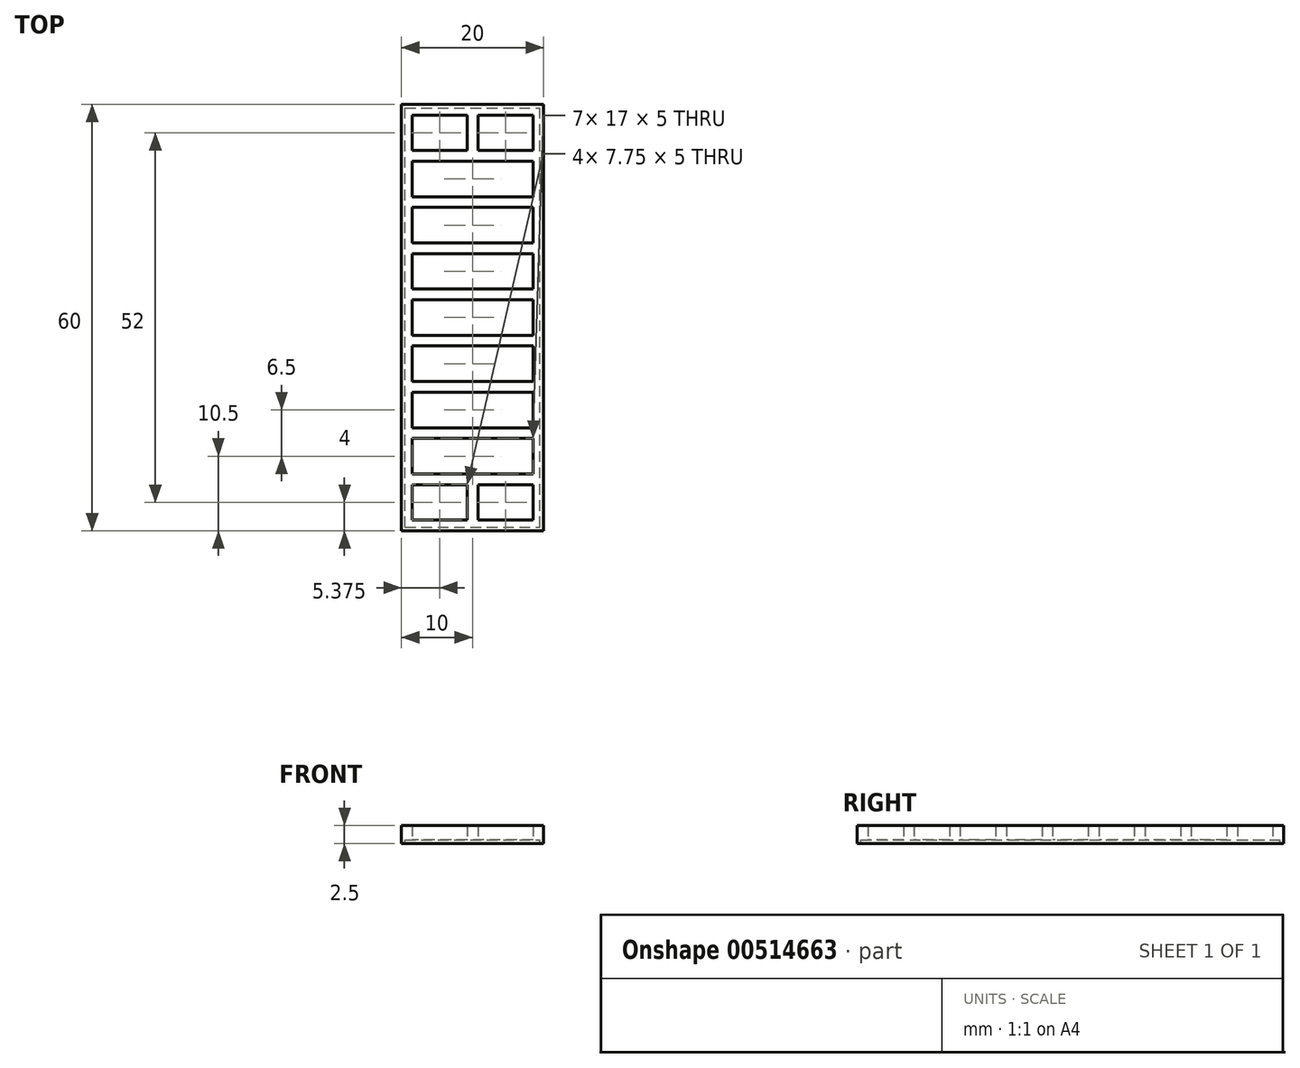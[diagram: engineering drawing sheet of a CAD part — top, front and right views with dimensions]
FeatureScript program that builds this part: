
annotation { "Feature Type Name" : "Feature", "Feature Type Description" : "" }
export const myFeature = defineFeature(function(context is Context, id is Id, definition is map)
    precondition{}
    {
        {
            var Q0;
            Q0=qCreatedBy(makeId("Top.planeOp"),FACE);
            var sketch = newSketch(context, id + "F0", { "sketchPlane" : qUnion([Q0])});
            skLineSegment(sketch, "E0.bottom", {"start": v(0, 0) * mm, "end": v(20, 0) * mm});
            skLineSegment(sketch, "E0.top", {"start": v(0, 60) * mm, "end": v(20, 60) * mm});
            skLineSegment(sketch, "E0.left", {"start": v(0, 0) * mm, "end": v(0, 60) * mm});
            skLineSegment(sketch, "E0.right", {"start": v(20, 0) * mm, "end": v(20, 60) * mm});
            skLineSegment(sketch, "E1.0", {"start": v(1.5, 1.5) * mm, "end": v(1.5, 6.5) * mm});
            skLineSegment(sketch, "E1.1", {"start": v(1.5, 1.5) * mm, "end": v(9.25, 1.5) * mm});
            skLineSegment(sketch, "E1.2", {"start": v(18.5, 1.5) * mm, "end": v(18.5, 6.5) * mm});
            skLineSegment(sketch, "E1.3", {"start": v(1.5, 58.5) * mm, "end": v(9.25, 58.5) * mm});
            skLineSegment(sketch, "E2", {"start": v(1.5, 53.5) * mm, "end": v(9.25, 53.5) * mm});
            skLineSegment(sketch, "E3", {"start": v(1.5, 52) * mm, "end": v(18.5, 52) * mm});
            skLineSegment(sketch, "E4.1.0.0", {"start": v(1.5, 47) * mm, "end": v(18.5, 47) * mm});
            skLineSegment(sketch, "E4.1.0.1", {"start": v(1.5, 45.5) * mm, "end": v(18.5, 45.5) * mm});
            skLineSegment(sketch, "E4.2.0.0", {"start": v(1.5, 40.5) * mm, "end": v(18.5, 40.5) * mm});
            skLineSegment(sketch, "E4.2.0.1", {"start": v(1.5, 39) * mm, "end": v(18.5, 39) * mm});
            skLineSegment(sketch, "E4.3.0.0", {"start": v(1.5, 34) * mm, "end": v(18.5, 34) * mm});
            skLineSegment(sketch, "E4.3.0.1", {"start": v(1.5, 32.5) * mm, "end": v(18.5, 32.5) * mm});
            skLineSegment(sketch, "E4.4.0.0", {"start": v(1.5, 27.5) * mm, "end": v(18.5, 27.5) * mm});
            skLineSegment(sketch, "E4.4.0.1", {"start": v(1.5, 26) * mm, "end": v(18.5, 26) * mm});
            skLineSegment(sketch, "E4.5.0.0", {"start": v(1.5, 21) * mm, "end": v(18.5, 21) * mm});
            skLineSegment(sketch, "E4.5.0.1", {"start": v(1.5, 19.5) * mm, "end": v(18.5, 19.5) * mm});
            skLineSegment(sketch, "E4.6.0.0", {"start": v(1.5, 14.5) * mm, "end": v(18.5, 14.5) * mm});
            skLineSegment(sketch, "E4.6.0.1", {"start": v(1.5, 13) * mm, "end": v(18.5, 13) * mm});
            skLineSegment(sketch, "E4.7.0.0", {"start": v(1.5, 8) * mm, "end": v(18.5, 8) * mm});
            skLineSegment(sketch, "E4.7.0.1", {"start": v(1.5, 6.5) * mm, "end": v(9.25, 6.5) * mm});
            skLineSegment(sketch, "E4.direction1", {"start": v(1.5, 52) * mm, "end": v(1.5, 47) * mm, "construction": true});
            skLineSegment(sketch, "E5", {"start": v(10.75, 58.5) * mm, "end": v(10.75, 53.5) * mm});
            skLineSegment(sketch, "E6", {"start": v(9.25, 58.5) * mm, "end": v(9.25, 53.5) * mm});
            skLineSegment(sketch, "E7", {"start": v(20, 30) * mm, "end": v(23.16, 30) * mm, "construction": true});
            skPoint(sketch, "E7.endSnap0", {"position": v(20, 30) * mm});
            skLineSegment(sketch, "E8.MirrorCS", {"start": v(10.75, 1.5) * mm, "end": v(10.75, 6.5) * mm});
            skLineSegment(sketch, "E9.MirrorCS", {"start": v(9.25, 1.5) * mm, "end": v(9.25, 6.5) * mm});
            skLineSegment(sketch, "E10.trimOffspring", {"start": v(10.75, 1.5) * mm, "end": v(18.5, 1.5) * mm});
            skLineSegment(sketch, "E11.trimOffspring", {"start": v(10.75, 6.5) * mm, "end": v(18.5, 6.5) * mm});
            skLineSegment(sketch, "E12.trimOffspring", {"start": v(18.5, 8) * mm, "end": v(18.5, 13) * mm});
            skLineSegment(sketch, "E13.trimOffspring", {"start": v(18.5, 14.5) * mm, "end": v(18.5, 19.5) * mm});
            skLineSegment(sketch, "E14.trimOffspring", {"start": v(1.5, 14.5) * mm, "end": v(1.5, 19.5) * mm});
            skLineSegment(sketch, "E15.trimOffspring", {"start": v(1.5, 8) * mm, "end": v(1.5, 13) * mm});
            skLineSegment(sketch, "E16.trimOffspring", {"start": v(18.5, 21) * mm, "end": v(18.5, 26) * mm});
            skLineSegment(sketch, "E17.trimOffspring", {"start": v(1.5, 21) * mm, "end": v(1.5, 26) * mm});
            skLineSegment(sketch, "E18.trimOffspring", {"start": v(1.5, 27.5) * mm, "end": v(1.5, 32.5) * mm});
            skLineSegment(sketch, "E19.trimOffspring", {"start": v(18.5, 27.5) * mm, "end": v(18.5, 32.5) * mm});
            skLineSegment(sketch, "E20.trimOffspring", {"start": v(18.5, 34) * mm, "end": v(18.5, 39) * mm});
            skLineSegment(sketch, "E21.trimOffspring", {"start": v(1.5, 34) * mm, "end": v(1.5, 39) * mm});
            skLineSegment(sketch, "E22.trimOffspring", {"start": v(18.5, 40.5) * mm, "end": v(18.5, 45.5) * mm});
            skLineSegment(sketch, "E23.trimOffspring", {"start": v(1.5, 40.5) * mm, "end": v(1.5, 45.5) * mm});
            skLineSegment(sketch, "E24.trimOffspring", {"start": v(1.5, 47) * mm, "end": v(1.5, 52) * mm});
            skLineSegment(sketch, "E25.trimOffspring", {"start": v(18.5, 53.5) * mm, "end": v(18.5, 58.5) * mm});
            skLineSegment(sketch, "E26.trimOffspring", {"start": v(1.5, 53.5) * mm, "end": v(1.5, 58.5) * mm});
            skLineSegment(sketch, "E27.trimOffspring", {"start": v(10.75, 53.5) * mm, "end": v(18.5, 53.5) * mm});
            skLineSegment(sketch, "E28.trimOffspring", {"start": v(10.75, 58.5) * mm, "end": v(18.5, 58.5) * mm});
            skPoint(sketch, "E29.orphan", {"position": v(10, 58.5) * mm});
            skLineSegment(sketch, "E30", {"start": v(18.5, 47) * mm, "end": v(18.5, 52) * mm});
            skSolve(sketch);
        }
        {
            var Q0;
            Q0 = qSketchRegion(id + "F0", true);
            extrude(context, id + "F1", {"entities" : qUnion([Q0]), "depth" : 2.5 * mm, "offsetDistance" : 25 * mm});
        }
        {
            var Q0;
            Q0=makeQuery(id+"F1.opExtrude","CAP_FACE",FACE,{"disambiguationData":[OSD([sQuery(id+"F0.wireOp",EDGE,"E0.bottom"),sQuery(id+"F0.wireOp",EDGE,"E0.top"),sQuery(id+"F0.wireOp",EDGE,"E0.left"),sQuery(id+"F0.wireOp",EDGE,"E0.right"),sQuery(id+"F0.wireOp",EDGE,"E1.0"),sQuery(id+"F0.wireOp",EDGE,"E1.1"),sQuery(id+"F0.wireOp",EDGE,"E1.2"),sQuery(id+"F0.wireOp",EDGE,"E1.3"),sQuery(id+"F0.wireOp",EDGE,"E2"),sQuery(id+"F0.wireOp",EDGE,"E3"),sQuery(id+"F0.wireOp",EDGE,"E4.1.0.0"),sQuery(id+"F0.wireOp",EDGE,"E4.1.0.1"),sQuery(id+"F0.wireOp",EDGE,"E4.2.0.0"),sQuery(id+"F0.wireOp",EDGE,"E4.2.0.1"),sQuery(id+"F0.wireOp",EDGE,"E4.3.0.0"),sQuery(id+"F0.wireOp",EDGE,"E4.3.0.1"),sQuery(id+"F0.wireOp",EDGE,"E4.4.0.0"),sQuery(id+"F0.wireOp",EDGE,"E4.4.0.1"),sQuery(id+"F0.wireOp",EDGE,"E4.5.0.0"),sQuery(id+"F0.wireOp",EDGE,"E4.5.0.1"),sQuery(id+"F0.wireOp",EDGE,"E4.6.0.0"),sQuery(id+"F0.wireOp",EDGE,"E4.6.0.1"),sQuery(id+"F0.wireOp",EDGE,"E4.7.0.0"),sQuery(id+"F0.wireOp",EDGE,"E4.7.0.1"),sQuery(id+"F0.wireOp",EDGE,"E5"),sQuery(id+"F0.wireOp",EDGE,"E6"),sQuery(id+"F0.wireOp",EDGE,"E8.MirrorCS"),sQuery(id+"F0.wireOp",EDGE,"E9.MirrorCS"),sQuery(id+"F0.wireOp",EDGE,"E10.trimOffspring"),sQuery(id+"F0.wireOp",EDGE,"E11.trimOffspring"),sQuery(id+"F0.wireOp",EDGE,"E12.trimOffspring"),sQuery(id+"F0.wireOp",EDGE,"E13.trimOffspring"),sQuery(id+"F0.wireOp",EDGE,"E14.trimOffspring"),sQuery(id+"F0.wireOp",EDGE,"E15.trimOffspring"),sQuery(id+"F0.wireOp",EDGE,"E16.trimOffspring"),sQuery(id+"F0.wireOp",EDGE,"E17.trimOffspring"),sQuery(id+"F0.wireOp",EDGE,"E18.trimOffspring"),sQuery(id+"F0.wireOp",EDGE,"E19.trimOffspring"),sQuery(id+"F0.wireOp",EDGE,"E20.trimOffspring"),sQuery(id+"F0.wireOp",EDGE,"E21.trimOffspring"),sQuery(id+"F0.wireOp",EDGE,"E22.trimOffspring"),sQuery(id+"F0.wireOp",EDGE,"E23.trimOffspring"),sQuery(id+"F0.wireOp",EDGE,"E24.trimOffspring"),sQuery(id+"F0.wireOp",EDGE,"E25.trimOffspring"),sQuery(id+"F0.wireOp",EDGE,"E26.trimOffspring"),sQuery(id+"F0.wireOp",EDGE,"E27.trimOffspring"),sQuery(id+"F0.wireOp",EDGE,"E28.trimOffspring"),sQuery(id+"F0.wireOp",EDGE,"E30")])],"isStart":true});
            var sketch = newSketch(context, id + "F2", { "sketchPlane" : qUnion([Q0])});
            skLineSegment(sketch, "E31", {"start": v(0, 0) * mm, "end": v(0, -0.5) * mm, "construction": true});
            skLineSegment(sketch, "E32", {"start": v(0, -0.5) * mm, "end": v(0.5, -0.5) * mm, "construction": true});
            skLineSegment(sketch, "E33", {"start": v(20, -60) * mm, "end": v(19.5, -60) * mm, "construction": true});
            skLineSegment(sketch, "E34", {"start": v(19.5, -60) * mm, "end": v(19.5, -59.5) * mm, "construction": true});
            skLineSegment(sketch, "E35.bottom", {"start": v(0.5, -0.5) * mm, "end": v(19.5, -0.5) * mm});
            skLineSegment(sketch, "E35.top", {"start": v(0.5, -59.5) * mm, "end": v(19.5, -59.5) * mm});
            skLineSegment(sketch, "E35.left", {"start": v(0.5, -0.5) * mm, "end": v(0.5, -59.5) * mm});
            skLineSegment(sketch, "E35.right", {"start": v(19.5, -0.5) * mm, "end": v(19.5, -59.5) * mm});
            skSolve(sketch);
        }
        {
            var Q0;
            Q0 = qSketchRegion(id + "F2", true);
            extrude(context, id + "F3", {"entities" : qUnion([Q0]), "operationType" : NewBodyOperationType.REMOVE, "oppositeDirection" : true, "depth" : 0.5 * mm, "offsetDistance" : 25 * mm});
        }
        {
            var Q0;
            Q0=makeQuery(id+"F3.boolean.opBoolean","COPY",FACE,{"derivedFrom":makeQuery(id+"F3.opExtrude","CAP_FACE",FACE,{"disambiguationData":[OSD([sQuery(id+"F2.wireOp",EDGE,"E35.bottom"),sQuery(id+"F2.wireOp",EDGE,"E35.top"),sQuery(id+"F2.wireOp",EDGE,"E35.left"),sQuery(id+"F2.wireOp",EDGE,"E35.right")])],"isStart":false})});
            var sketch = newSketch(context, id + "F4", { "sketchPlane" : qUnion([Q0])});
            skLineSegment(sketch, "E36.bottom", {"start": v(0.5, -0.5) * mm, "end": v(19.5, -0.5) * mm});
            skLineSegment(sketch, "E36.top", {"start": v(0.5, -59.5) * mm, "end": v(19.5, -59.5) * mm});
            skLineSegment(sketch, "E36.left", {"start": v(0.5, -0.5) * mm, "end": v(0.5, -59.5) * mm});
            skLineSegment(sketch, "E36.right", {"start": v(19.5, -0.5) * mm, "end": v(19.5, -59.5) * mm});
            skSolve(sketch);
        }
        {
            var Q0;
            Q0 = qSketchRegion(id + "F4", true);
            extrude(context, id + "F5", {"entities" : qUnion([Q0]), "depth" : 0.5 * mm, "offsetDistance" : 25 * mm});
        }
    });
